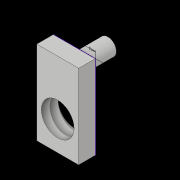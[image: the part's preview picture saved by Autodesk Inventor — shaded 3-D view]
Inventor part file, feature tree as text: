
AUTODESK INVENTOR PART (.ipt)
format: ipt  version: 2017 (Build 210142000, 142)  size: 107,520 bytes
history: native  units: in
note: dims shown in document units (in); Inventor stores cm internally (conversion verified against a paired STEP export)
features: sketch x2, extrude x2, hole x1
ambient origin geometry x8: Origin, YZ Plane, XZ Plane, XY Plane, X Axis, Y Axis, Z Axis, Center Point
bodies: Solid1 (feature_tree)
feature tree (5):
  sketch  "Sketch1"  dims[d0=0.25in d1=0.5in]
  extrude  "Extrusion1"  Depth=0.5in
  extrude  "Extrusion2"  Depth=0.1in
  hole  "Hole1"  [1 undecoded]
  sketch  "Sketch2"  dims[d3=0.1in d4=0.0in d5=0.1in d6=0.1in d7=0.125in d8=0.3in d9=0.0in d11=0.196in d12=0.5in d13=0.375in d14=0.25in d15=0.5635in d16=0.75in d17=0.8108in]
note: 1 required parameter value undecoded (feature->parameter linkage not recoverable at this tier; creation-order binding heuristic only, values carry confidence <= 0.55)
